# Revit family: Plumbing_Drainage_Menzies-Metal_Clamp-Tite_Copper-Drain-TPO_No-Hub
name_source: partatom
category: Plumbing Fixtures
revit_build: Autodesk Revit 2018 (Build: 20170223_1515(x64)
units: mm (PartAtom-declared; Revit-internal decimal feet)

## family parameters
Cut with Voids When Loaded = No
Host = Face
OmniClass Number = 23.70.50.21.24.11
OmniClass Title = Roof Waste Water Drains
Part Type = Normal
Room Calculation Point = No
Round Connector Dimension = Use Diameter
Shared = No

## types (3) — shared parameters
Assembly Code = D2040200
Connector = Standard sized couplers. Not supplied by manufacturer
Default Elevation = 4' - 0"
Description = Clamp-Tite Spun Copper Drain No Hub TPO
Drain Flow = 0 GPM
Edition number = 1
Manufacturer = Menzies Metal Products
Product Guid = b2ac0273-2f91-42be-8c76-979c71e526d7
Product Material = Metal - Menzies Metal Products - Copper TPO Coated
Product data url = https://www.bimobject.com
URL = https://www.menzies-metal.com

## per-type parameters (varying)
| type | Model | Pipe Length | Weight |
| 2" | 300-3180TPO | 0' - 4 1/2" | 3.61 lbf |
| 3" | 300-3185TPO | 0' - 4 1/2" | 3.87 lbf |
| 4" | 300-3190TPO | 0' - 3 3/4" | 4.48 lbf |

note: column(s) folded — value = type name in every type: Pipe Diameter

## geometry (parser evidence)
native form markers: Sweep x3
no freeform markers — native parametric forms only
